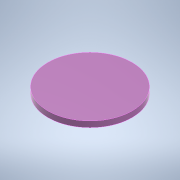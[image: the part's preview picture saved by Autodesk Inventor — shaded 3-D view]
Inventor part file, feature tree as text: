
AUTODESK INVENTOR PART (.ipt)
format: ipt  version: 2021 (Build 250183000, 183)  size: 111,616 bytes
history: native  units: mm
features: extrude x1, sketch x1
ambient origin geometry x8: Origin, YZ Plane, XZ Plane, XY Plane, X Axis, Y Axis, Z Axis, Center Point
bodies: Solid1 (feature_tree)
feature tree (2):
  extrude  "Extrusion1"  Depth=1.75mm TaperAngle=0.0deg
  sketch  "Sketch1"  dims[d0=25.25mm d1=1.75mm d2=0.0mm]
